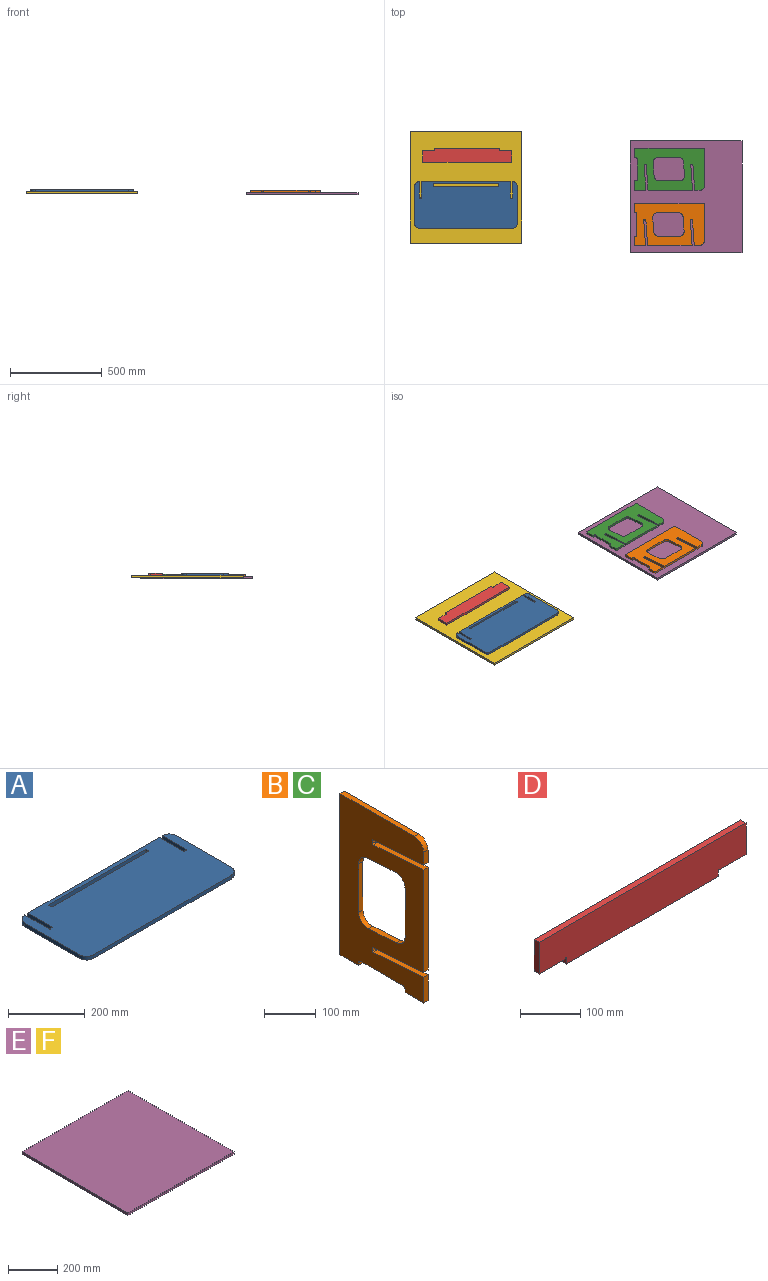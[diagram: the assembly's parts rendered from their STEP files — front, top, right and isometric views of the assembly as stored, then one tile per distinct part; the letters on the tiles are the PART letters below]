
ASSEMBLY  parts=6 mates=4
PART A: 28 faces, bbox 558.8x254x12 mm
  f0: plane 508x12mm, normal (0,-1,0), area 6096mm2, adj f1,f17,f18,f19
  f1: cylinder r=25.4mm len=25.4mm, axis (0,0,-1), area 478.8mm2, adj f0,f2,f18,f19
  f2: plane 203.2x12mm, normal (1,0,0), area 2438.4mm2, adj f1,f3,f18,f19
  f3: cylinder r=25.4mm len=25.4mm, axis (0,0,-1), area 478.8mm2, adj f2,f4,f18,f19
  f4: plane 90.22x12mm, normal (-1,0,0), area 1082.6mm2, adj f3,f5,f18,f19
  f5: cylinder r=1.6mm len=12mm, axis (0,0,-1), area 60.3mm2, adj f4,f6,f18,f19
  f6: plane 12x5.1mm, normal (0,1,0), area 61.2mm2, adj f5,f7,f18,f19
  f7: cylinder r=1.6mm len=12mm, axis (0,0,-1), area 60.3mm2, adj f6,f8,f18,f19
  f8: plane 90.22x12mm, normal (1,0,0), area 1082.6mm2, adj f7,f9,f18,f19
  f9: plane 485x12mm, normal (0,1,0), area 5820mm2, adj f8,f10,f18,f19
  f10: plane 90.22x12mm, normal (-1,0,0), area 1082.6mm2, adj f9,f11,f18,f19
  f11: cylinder r=1.6mm len=12mm, axis (0,0,-1), area 78.9mm2, adj f10,f12,f18,f19
  f12: plane 12x6.49mm, normal (0,1,0), area 77.9mm2, adj f11,f13,f18,f19
  f13: cylinder r=1.6mm len=12mm, axis (0,0,-1), area 78.9mm2, adj f12,f14,f18,f19
  f14: plane 90.22x12mm, normal (1,0,0), area 1082.6mm2, adj f13,f15,f18,f19
  f15: cylinder r=25.4mm len=25.4mm, axis (0,0,-1), area 478.8mm2, adj f14,f16,f18,f19
  f16: plane 203.2x12mm, normal (-1,0,0), area 2438.4mm2, adj f15,f17,f18,f19
  f17: cylinder r=25.4mm len=25.4mm, axis (0,0,-1), area 478.8mm2, adj f0,f16,f18,f19
  f18: plane 558.8x254mm, normal (0,0,1), area 135192mm2, adj f0,f1,f2,f3,f4,f5,f6,f7
  f19: plane 558.8x254mm, normal (0,0,-1), area 135192mm2, adj f0,f1,f2,f3,f4,f5,f6,f7
  f20: cylinder r=1.6mm len=12mm, axis (0,0,1), area 60.3mm2, adj f18,f19,f21,f27
  f21: plane 355.6x12mm, normal (0,1,0), area 4267.2mm2, adj f18,f19,f20,f22
  f22: cylinder r=1.6mm len=12mm, axis (0,0,1), area 60.3mm2, adj f18,f19,f21,f23
  f23: plane 12x5.1mm, normal (-1,0,0), area 61.2mm2, adj f18,f19,f22,f24
  f24: cylinder r=1.6mm len=12mm, axis (0,0,1), area 60.3mm2, adj f18,f19,f23,f25
  f25: plane 355.6x12mm, normal (0,-1,0), area 4267.2mm2, adj f18,f19,f24,f26
  f26: cylinder r=1.6mm len=12mm, axis (0,0,1), area 60.3mm2, adj f18,f19,f25,f27
  f27: plane 12x5.1mm, normal (1,0,0), area 61.2mm2, adj f18,f19,f20,f26
PART B: 33 faces, bbox 12x228.6x381 mm
  f0: plane 50.8x12mm, normal (0,0,-1), area 609.6mm2, adj f1,f3,f18,f23
  f1: plane 381x228.6mm, normal (1,0,0), area 61673.5mm2, adj f0,f2,f3,f4,f5,f6,f7,f8
  f2: plane 138.56x12mm, normal (0,0.07,1), area 1666.8mm2, adj f1,f3,f17,f18
  f3: plane 60.49x12mm, normal (0,-1,0), area 725.9mm2, adj f0,f1,f2,f18
  f4: plane 50.8x12mm, normal (0,0,-1), area 609.6mm2, adj f1,f5,f18,f20
  f5: plane 381x12mm, normal (0,1,0), area 4572mm2, adj f1,f4,f6,f18
  f6: plane 203.2x12mm, normal (0,0,1), area 2438.4mm2, adj f1,f5,f18,f19
  f7: plane 29.58x12mm, normal (0,-1,0), area 355mm2, adj f1,f8,f18,f19
  f8: plane 139.36x12mm, normal (0,-0.07,-1), area 1676.4mm2, adj f1,f7,f9,f18
  f9: cylinder r=1.6mm len=12mm, axis (-1,0,0), area 60.3mm2, adj f1,f8,f10,f18
  f10: plane 12x5.09mm, normal (0,-1,0.07), area 61.2mm2, adj f1,f9,f11,f18
  f11: cylinder r=1.6mm len=12mm, axis (-1,0,0), area 60.3mm2, adj f1,f10,f12,f18
  f12: plane 138.56x12mm, normal (0,0.07,1), area 1666.8mm2, adj f1,f11,f13,f18
  f13: plane 242.47x12mm, normal (0,-1,0), area 2909.7mm2, adj f1,f12,f14,f18
  f14: plane 139.36x12mm, normal (0,-0.07,-1), area 1676.4mm2, adj f1,f13,f15,f18
  f15: cylinder r=1.6mm len=12mm, axis (-1,0,0), area 60.3mm2, adj f1,f14,f16,f18
  f16: plane 12x5.09mm, normal (0,-1,0.07), area 61.2mm2, adj f1,f15,f17,f18
  f17: cylinder r=1.6mm len=12mm, axis (-1,0,0), area 60.3mm2, adj f1,f2,f16,f18
  f18: plane 381x228.6mm, normal (-1,0,0), area 61673.5mm2, adj f0,f2,f3,f4,f5,f6,f7,f8
  f19: cylinder r=25.4mm len=25.4mm, axis (-1,0,0), area 478.8mm2, adj f1,f6,f7,f18
  f20: plane 12x6.35mm, normal (0,-1,0), area 76.2mm2, adj f1,f4,f18,f21
  f21: cylinder r=6.35mm len=12mm, axis (1,0,0), area 119.7mm2, adj f1,f18,f20,f22
  f22: plane 114.3x12mm, normal (0,0,-1), area 1371.6mm2, adj f1,f18,f21,f24
  f23: plane 12x6.35mm, normal (0,1,0), area 76.2mm2, adj f0,f1,f18,f24
  f24: cylinder r=6.35mm len=12mm, axis (1,0,0), area 119.7mm2, adj f1,f18,f22,f23
  f25: plane 114.66x12mm, normal (0,-1,0), area 1375.9mm2, adj f1,f18,f26,f32
  f26: cylinder r=25.4mm len=25.34mm, axis (1,0,0), area 457.5mm2, adj f1,f18,f25,f27
  f27: plane 76.2x12mm, normal (0,-0.07,-1), area 916.6mm2, adj f1,f18,f26,f28
  f28: cylinder r=25.4mm len=27.17mm, axis (1,0,0), area 500.1mm2, adj f1,f18,f27,f29
  f29: plane 114.66x12mm, normal (0,1,0), area 1375.9mm2, adj f1,f18,f28,f30
  f30: cylinder r=25.4mm len=25.34mm, axis (1,0,0), area 457.5mm2, adj f1,f18,f29,f31
  f31: plane 76.2x12mm, normal (0,0.07,1), area 916.6mm2, adj f1,f18,f30,f32
  f32: cylinder r=25.4mm len=27.17mm, axis (1,0,0), area 500.1mm2, adj f1,f18,f25,f31
PART C: same geometry as B
PART D: 12 faces, bbox 484.8x12x76.2 mm
  f0: cylinder r=1.6mm len=12mm, axis (0,1,0), area 60.3mm2, adj f1,f9,f10,f11
  f1: plane 12x12mm, normal (-1,0,0), area 144mm2, adj f0,f2,f10,f11
  f2: plane 355.6x12mm, normal (0,0,-1), area 4267.2mm2, adj f1,f3,f10,f11
  f3: plane 12x12mm, normal (1,0,0), area 144mm2, adj f2,f4,f10,f11
  f4: cylinder r=1.6mm len=12mm, axis (0,1,0), area 60.3mm2, adj f3,f5,f10,f11
  f5: plane 61.38x12mm, normal (0,0,-1), area 736.6mm2, adj f4,f6,f10,f11
  f6: plane 64.2x12mm, normal (1,0,0), area 770.4mm2, adj f5,f7,f10,f11
  f7: plane 484.76x12mm, normal (0,0,1), area 5817.1mm2, adj f6,f8,f10,f11
  f8: plane 64.2x12mm, normal (-1,0,0), area 770.4mm2, adj f7,f9,f10,f11
  f9: plane 61.38x12mm, normal (0,0,-1), area 736.6mm2, adj f0,f8,f10,f11
  f10: plane 484.76x76.2mm, normal (0,-1,0), area 35380.9mm2, adj f0,f1,f2,f3,f4,f5,f6,f7
  f11: plane 484.76x76.2mm, normal (0,1,0), area 35380.9mm2, adj f0,f1,f2,f3,f4,f5,f6,f7
PART E: 6 faces, bbox 609.6x609.6x12 mm
  f0: plane 609.6x12mm, normal (0,1,0), area 7315.2mm2, adj f1,f3,f4,f5
  f1: plane 609.6x12mm, normal (-1,0,0), area 7315.2mm2, adj f0,f2,f4,f5
  f2: plane 609.6x12mm, normal (0,-1,0), area 7315.2mm2, adj f1,f3,f4,f5
  f3: plane 609.6x12mm, normal (1,0,0), area 7315.2mm2, adj f0,f2,f4,f5
  f4: plane 609.6x609.6mm, normal (0,0,1), area 371612.2mm2, adj f0,f1,f2,f3
  f5: plane 609.6x609.6mm, normal (0,0,-1), area 371612.2mm2, adj f0,f1,f2,f3
PART F: same geometry as E
PLACE A t=(0,-96.32,12)mm
PLACE B rot(axis=(0,1,0),90deg) t=(1108.28,-203.04,18)mm
PLACE C rot(axis=(0,1,0),90deg) t=(1110.49,98.44,18)mm
PLACE D rot(axis=(1,0,0),90deg) t=(6.89,167.02,24)mm
PLACE E t=(1199.11,-51.92,-6)mm fixed
PLACE F at identity fixed
MATE planar E.f4 <-> C.f1  axis (0,0,1) through (1199.11,-51.92,6)mm
MATE planar A.f19 <-> F.f4  axis (0,0,-1) through (-0.01,-100.87,12)mm
MATE planar B.f1 <-> E.f4  axis (0,0,-1) through (1114.48,-200.48,6)mm
MATE planar D.f10 <-> F.f4  axis (0,0,-1) through (6.89,211.12,12)mm
